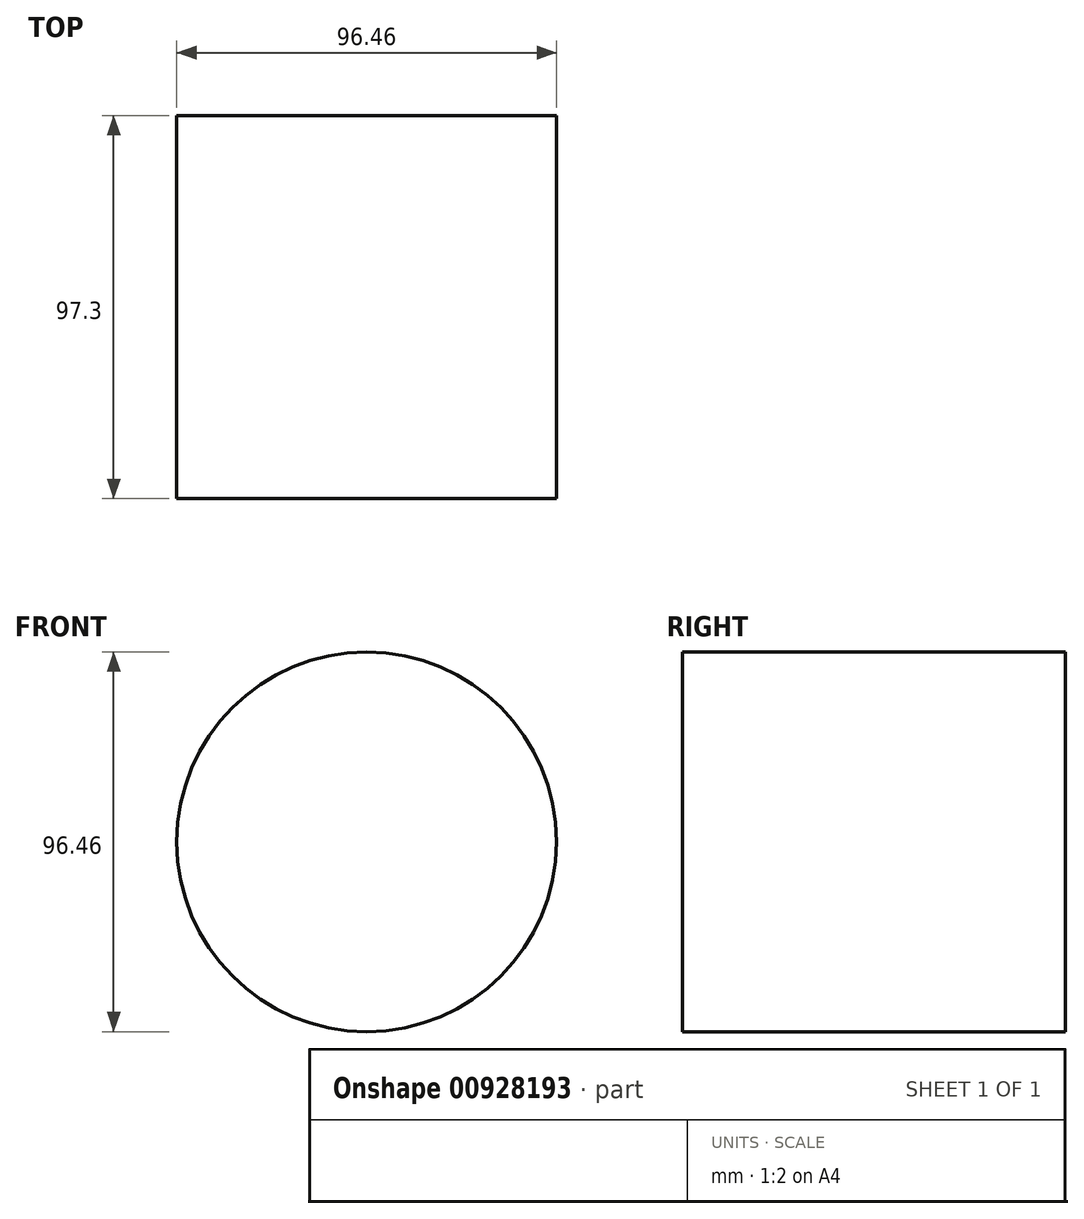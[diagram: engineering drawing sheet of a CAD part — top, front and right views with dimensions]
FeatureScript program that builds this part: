
annotation { "Feature Type Name" : "Feature", "Feature Type Description" : "" }
export const myFeature = defineFeature(function(context is Context, id is Id, definition is map)
    precondition{}
    {
        {
            var Q0;
            Q0=qCreatedBy(makeId("Front.planeOp"),FACE);
            var sketch = newSketch(context, id + "F0", { "sketchPlane" : qUnion([Q0])});
            skCircle(sketch, "E0", {"center": v(0, 0) * mm, "radius": 48.23 * mm});
            skSolve(sketch);
        }
        {
            var Q0;
            Q0=makeQuery(id+"F0.imprint","IMPRINT",FACE,{"disambiguationData":[TD([[makeQuery(id+"F0.imprint","IMPRINT",EDGE,{"derivedFrom":sQuery(id+"F0.wireOp",EDGE,"E0")}),1.0]])]});
            extrude(context, id + "F1", {"entities" : qUnion([Q0]), "depth" : 97.3 * mm, "offsetDistance" : 25 * mm});
        }
    });
